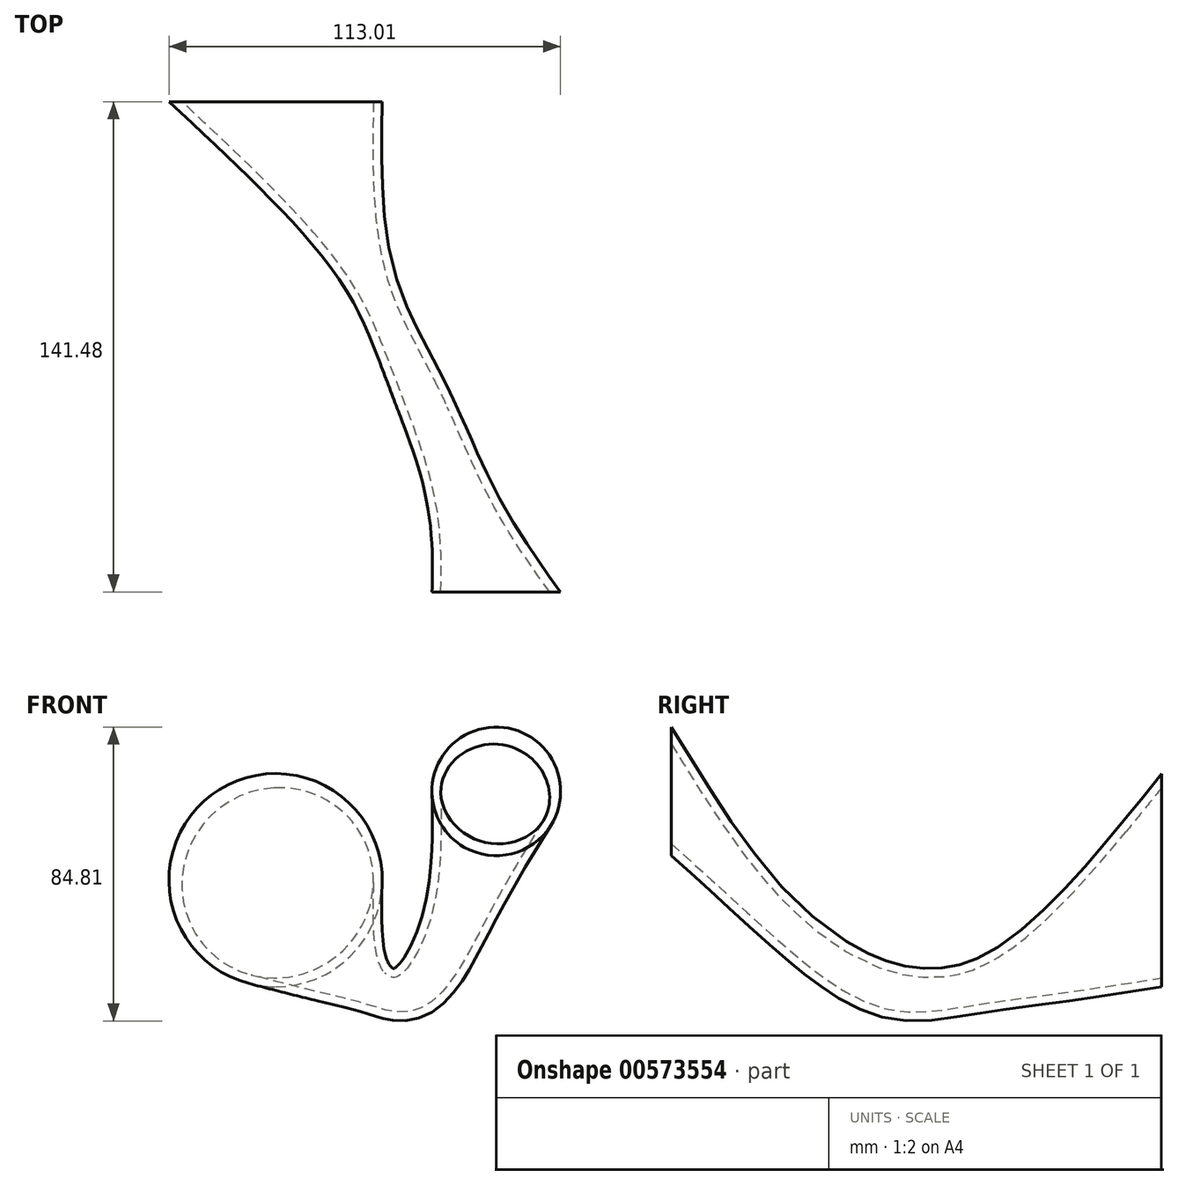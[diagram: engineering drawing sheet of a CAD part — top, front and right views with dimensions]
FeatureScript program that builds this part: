
annotation { "Feature Type Name" : "Feature", "Feature Type Description" : "" }
export const myFeature = defineFeature(function(context is Context, id is Id, definition is map)
    precondition{}
    {
        {
            var Q0;
            Q0=qCreatedBy(makeId("Front.planeOp"),FACE);
            var sketch = newSketch(context, id + "F0", { "sketchPlane" : qUnion([Q0])});
            skCircle(sketch, "E0", {"center": v(-38.59, 32.25) * mm, "radius": 30.77 * mm});
            skSolve(sketch);
        }
        {
            var Q0;
            Q0=qCreatedBy(makeId("Front.planeOp"),FACE);
            cPlane(context, id + "F1", {"entities" : qUnion([Q0]), "cplaneType" : CPlaneType.OFFSET, "offset" : 76.45 * mm, "width" : 152.4 * mm, "height" : 152.4 * mm});
        }
        {
            var Q0;
            Q0=qCreatedBy(id+"F1.planeOp",FACE);
            var sketch = newSketch(context, id + "F2", { "sketchPlane" : qUnion([Q0])});
            skCircle(sketch, "E1", {"center": v(0, 0) * mm, "radius": 8.05 * mm});
            skSolve(sketch);
        }
        {
            var Q0;
            Q0=qCreatedBy(id+"F1.planeOp",FACE);
            cPlane(context, id + "F3", {"entities" : qUnion([Q0]), "cplaneType" : CPlaneType.OFFSET, "offset" : 65.02 * mm, "width" : 152.4 * mm, "height" : 152.4 * mm});
        }
        {
            var Q0;
            Q0=qCreatedBy(id+"F3.planeOp",FACE);
            var sketch = newSketch(context, id + "F4", { "sketchPlane" : qUnion([Q0])});
            skCircle(sketch, "E2", {"center": v(25.1, 57.88) * mm, "radius": 18.56 * mm});
            skSolve(sketch);
        }
        {
            var Q0;
            Q0=makeQuery(id+"F0.imprint","IMPRINT",FACE,{"disambiguationData":[TD([[makeQuery(id+"F0.imprint","IMPRINT",EDGE,{"derivedFrom":sQuery(id+"F0.wireOp",EDGE,"E0")}),1.0]])]});
            var Q1;
            Q1=makeQuery(id+"F2.imprint","IMPRINT",FACE,{"disambiguationData":[TD([[makeQuery(id+"F2.imprint","IMPRINT",EDGE,{"derivedFrom":sQuery(id+"F2.wireOp",EDGE,"E1")}),1.0]])]});
            var Q2;
            Q2=makeQuery(id+"F4.imprint","IMPRINT",FACE,{"disambiguationData":[TD([[makeQuery(id+"F4.imprint","IMPRINT",EDGE,{"derivedFrom":sQuery(id+"F4.wireOp",EDGE,"E2")}),1.0]])]});
            loft(context, id + "F5", {"sheetProfilesArray" : [{ "sheetProfileEntities" : qUnion([Q0]) }, { "sheetProfileEntities" : qUnion([Q1]) }, { "sheetProfileEntities" : qUnion([Q2]) }]});
        }
        {
            var Q0;
            Q0=makeQuery(id+"F5.opLoft","CAP_FACE",FACE,{"disambiguationData":[OSD([makeQuery(id+"F0.imprint","IMPRINT",FACE,{"disambiguationData":[TD([[makeQuery(id+"F0.imprint","IMPRINT",EDGE,{"derivedFrom":sQuery(id+"F0.wireOp",EDGE,"E0")}),1.0]])]})])],"isStart":true});
            var Q1;
            Q1=makeQuery(id+"F5.opLoft","CAP_FACE",FACE,{"disambiguationData":[OSD([makeQuery(id+"F4.imprint","IMPRINT",FACE,{"disambiguationData":[TD([[makeQuery(id+"F4.imprint","IMPRINT",EDGE,{"derivedFrom":sQuery(id+"F4.wireOp",EDGE,"E2")}),1.0]])]})])],"isStart":true});
            shell(context, id + "F6", {"entities" : qUnion([Q0, Q1]), "thickness" : 2.54 * mm});
        }
    });
